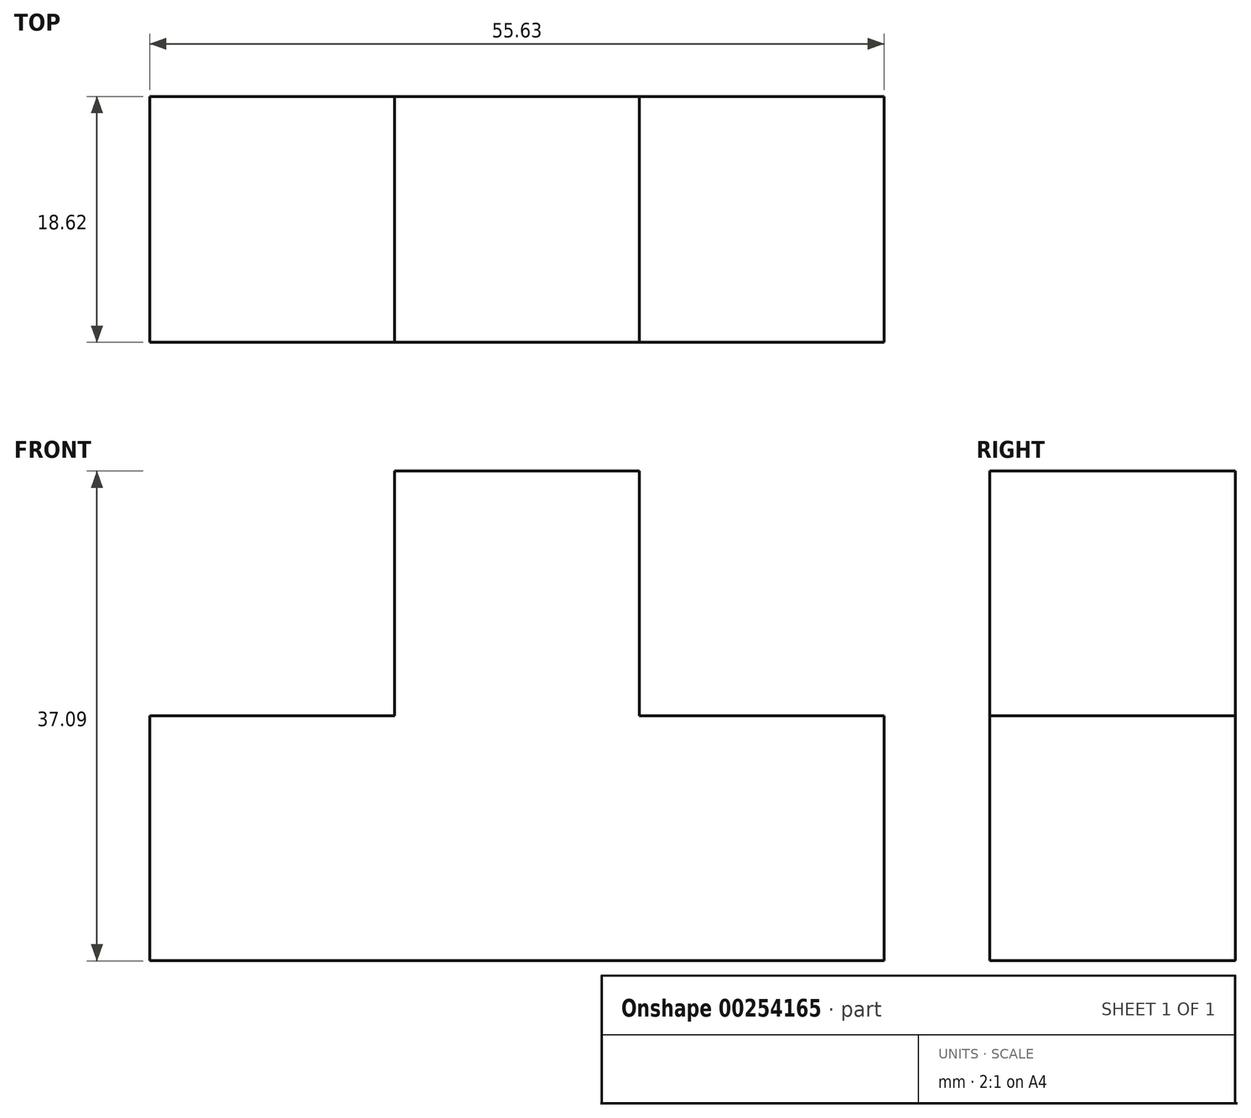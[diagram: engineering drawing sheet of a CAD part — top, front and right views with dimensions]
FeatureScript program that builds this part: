
annotation { "Feature Type Name" : "Feature", "Feature Type Description" : "" }
export const myFeature = defineFeature(function(context is Context, id is Id, definition is map)
    precondition{}
    {
        {
            var Q0;
            Q0=qCreatedBy(makeId("Front.planeOp"),FACE);
            var sketch = newSketch(context, id + "F0", { "sketchPlane" : qUnion([Q0])});
            skLineSegment(sketch, "E0.bottom", {"start": v(-46.04, -31.44) * mm, "end": v(-27.5, -31.44) * mm});
            skLineSegment(sketch, "E0.top", {"start": v(-46.04, -12.9) * mm, "end": v(-27.5, -12.9) * mm});
            skLineSegment(sketch, "E0.left", {"start": v(-46.04, -31.44) * mm, "end": v(-46.04, -12.9) * mm});
            skLineSegment(sketch, "E0.right", {"start": v(-27.5, -31.44) * mm, "end": v(-27.5, -12.9) * mm});
            skLineSegment(sketch, "E1.MirrorCS", {"start": v(-8.95, -12.9) * mm, "end": v(-27.5, -12.9) * mm});
            skLineSegment(sketch, "E2.MirrorCS", {"start": v(-8.95, -31.44) * mm, "end": v(-8.95, -12.9) * mm});
            skLineSegment(sketch, "E3.MirrorCS", {"start": v(-8.95, -31.44) * mm, "end": v(-27.5, -31.44) * mm});
            skLineSegment(sketch, "E4.MirrorCS", {"start": v(-8.95, -31.44) * mm, "end": v(9.59, -31.44) * mm});
            skLineSegment(sketch, "E5.MirrorCS", {"start": v(9.59, -31.44) * mm, "end": v(9.59, -12.9) * mm});
            skLineSegment(sketch, "E6.MirrorCS", {"start": v(-8.95, -12.9) * mm, "end": v(9.59, -12.9) * mm});
            skLineSegment(sketch, "E7.MirrorCS", {"start": v(-27.5, 5.65) * mm, "end": v(-27.5, -12.9) * mm});
            skLineSegment(sketch, "E8.MirrorCS", {"start": v(-8.95, 5.65) * mm, "end": v(-27.5, 5.65) * mm});
            skLineSegment(sketch, "E9.MirrorCS", {"start": v(-8.95, 5.65) * mm, "end": v(-8.95, -12.9) * mm});
            skSolve(sketch);
        }
        {
            var Q0;
            Q0 = qSketchRegion(id + "F0", true);
            extrude(context, id + "F1", {"entities" : qUnion([Q0]), "depth" : 18.62 * mm});
        }
    });
